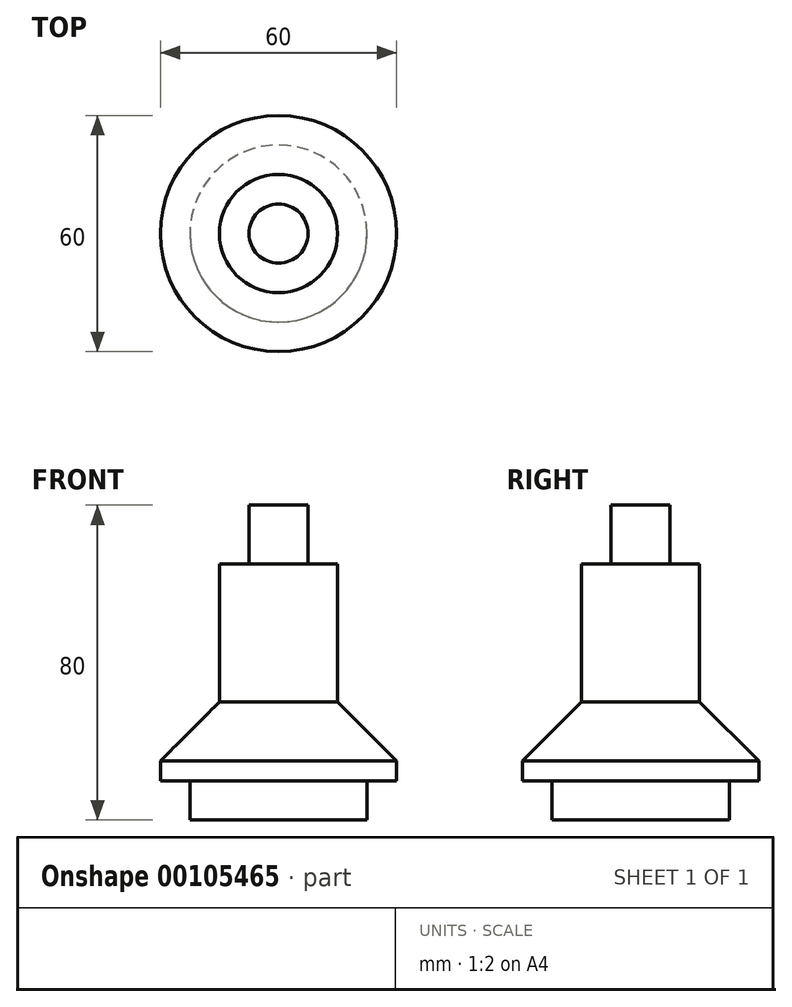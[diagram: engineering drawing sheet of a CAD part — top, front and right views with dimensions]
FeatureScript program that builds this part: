
annotation { "Feature Type Name" : "Feature", "Feature Type Description" : "" }
export const myFeature = defineFeature(function(context is Context, id is Id, definition is map)
    precondition{}
    {
        {
            var Q0;
            Q0=qCreatedBy(makeId("Top.planeOp"),FACE);
            var sketch = newSketch(context, id + "F0", { "sketchPlane" : qUnion([Q0])});
            skCircle(sketch, "E0", {"center": v(0, 0) * mm, "radius": 22.5 * mm});
            skSolve(sketch);
        }
        {
            var Q0;
            Q0=makeQuery(id+"F0.imprint","IMPRINT",FACE,{"disambiguationData":[TD([[makeQuery(id+"F0.imprint","IMPRINT",EDGE,{"derivedFrom":sQuery(id+"F0.wireOp",EDGE,"E0")}),1.0]])]});
            extrude(context, id + "F1", {"entities" : qUnion([Q0]), "depth" : 15 * mm});
        }
        {
            var Q0;
            Q0=qCreatedBy(makeId("Front.planeOp"),FACE);
            var sketch = newSketch(context, id + "F2", { "sketchPlane" : qUnion([Q0])});
            skLineSegment(sketch, "E1", {"start": v(0, 0) * mm, "end": v(0, 15) * mm});
            skLineSegment(sketch, "E2", {"start": v(0, 15) * mm, "end": v(-30, 15) * mm});
            skLineSegment(sketch, "E3", {"start": v(-30, 15) * mm, "end": v(-15, 30) * mm});
            skLineSegment(sketch, "E4", {"start": v(0, 15) * mm, "end": v(0, 30) * mm});
            skLineSegment(sketch, "E5", {"start": v(0, 30) * mm, "end": v(-15, 30) * mm});
            skSolve(sketch);
        }
        {
            var Q0;
            Q0=makeQuery(id+"F2.imprint","IMPRINT",FACE,{"disambiguationData":[TD([[makeQuery(id+"F2.imprint","IMPRINT",EDGE,{"derivedFrom":sQuery(id+"F2.wireOp",EDGE,"E2")}),-1.0]])]});
            var Q1;
            Q1=sQuery(id+"F2.wireOp",EDGE,"E1");
            revolve(context, id + "F3", {"operationType" : NewBodyOperationType.ADD, "entities" : qUnion([Q0]), "axis" : qUnion([Q1]), "revolveType" : RevolveType.FULL});
        }
        {
            var Q0;
            Q0=makeQuery(id+"F3.opRevolve","SWEPT_FACE",FACE,{"disambiguationData":[OSD([sQuery(id+"F2.wireOp",EDGE,"E2")])]});
            var sketch = newSketch(context, id + "F4", { "sketchPlane" : qUnion([Q0])});
            skCircle(sketch, "E6", {"center": v(0, 0) * mm, "radius": 30 * mm});
            skPoint(sketch, "E6.first.point", {"position": v(29.94, -1.94) * mm});
            skPoint(sketch, "E6.second.point", {"position": v(-29.67, 4.43) * mm});
            skPoint(sketch, "E6.third.point", {"position": v(10.92, 27.94) * mm});
            skSolve(sketch);
        }
        {
            var Q0;
            Q0 = qSketchRegion(id + "F4", true);
            extrude(context, id + "F5", {"entities" : qUnion([Q0]), "operationType" : NewBodyOperationType.ADD, "depth" : 5 * mm});
        }
        {
            var Q0;
            Q0=makeQuery(id+"F3.opRevolve","SWEPT_FACE",FACE,{"disambiguationData":[OSD([sQuery(id+"F2.wireOp",EDGE,"E5")])]});
            var sketch = newSketch(context, id + "F6", { "sketchPlane" : qUnion([Q0])});
            skCircle(sketch, "E7", {"center": v(0, 0) * mm, "radius": 15 * mm});
            skSolve(sketch);
        }
        {
            var Q0;
            Q0 = qSketchRegion(id + "F6", true);
            extrude(context, id + "F7", {"entities" : qUnion([Q0]), "operationType" : NewBodyOperationType.ADD, "depth" : 35 * mm});
        }
        {
            var Q0;
            Q0=makeQuery(id+"F7.opExtrude","CAP_FACE",FACE,{"disambiguationData":[OSD([sQuery(id+"F6.wireOp",EDGE,"E7")])],"isStart":false});
            var sketch = newSketch(context, id + "F8", { "sketchPlane" : qUnion([Q0])});
            skCircle(sketch, "E8", {"center": v(0, 0) * mm, "radius": 7.5 * mm});
            skSolve(sketch);
        }
        {
            var Q0;
            Q0 = qSketchRegion(id + "F8", true);
            extrude(context, id + "F9", {"entities" : qUnion([Q0]), "operationType" : NewBodyOperationType.ADD, "depth" : 15 * mm});
        }
    });
